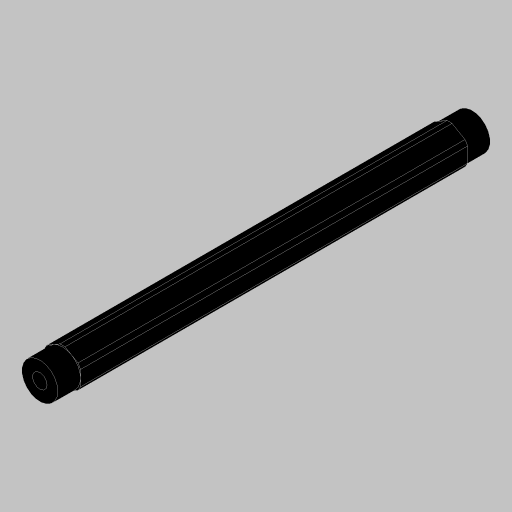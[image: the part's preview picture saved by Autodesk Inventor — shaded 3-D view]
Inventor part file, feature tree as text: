
AUTODESK INVENTOR PART (.ipt)
format: ipt  version: 2023.5 (Build 275446000, 446)  size: 162,304 bytes
history: native  units: in
note: dims shown in document units (in); Inventor stores cm internally (conversion verified against a paired STEP export)
features: extrude x3, projected_geometry x3, hole x1, mirror x1, sketch x1
ambient origin geometry x8: Origin, YZ Plane, XZ Plane, XY Plane, X Axis, Y Axis, Z Axis, Center Point
bodies: Solid1 (feature_tree)
feature tree (9):
  extrude  "Extrusion1"  Depth=0.315in
  hole  "Hole1"  [1 undecoded]
  extrude  "Extrusion3"  Depth=0.5in
  extrude  "Extrusion4"  Depth=0.315in TaperAngle=0.0deg
  mirror  "Mirror2"
  sketch  "Sketch5"  dims[d2=0.0in d9=0.625in d10=0.385in d11=0.25in d12=0.5635in d13=1.0in d14=0.8108in d16=0.7in d17=0.0in d18=0.0in d19=0.5in d20=0.315in d21=0.0in]
  projected_geometry  "Projected Loop2"
  projected_geometry  "Project Cut Edges1"
  projected_geometry  "Project Cut Edges2"
note: 1 required parameter value undecoded (feature->parameter linkage not recoverable at this tier; creation-order binding heuristic only, values carry confidence <= 0.55)
